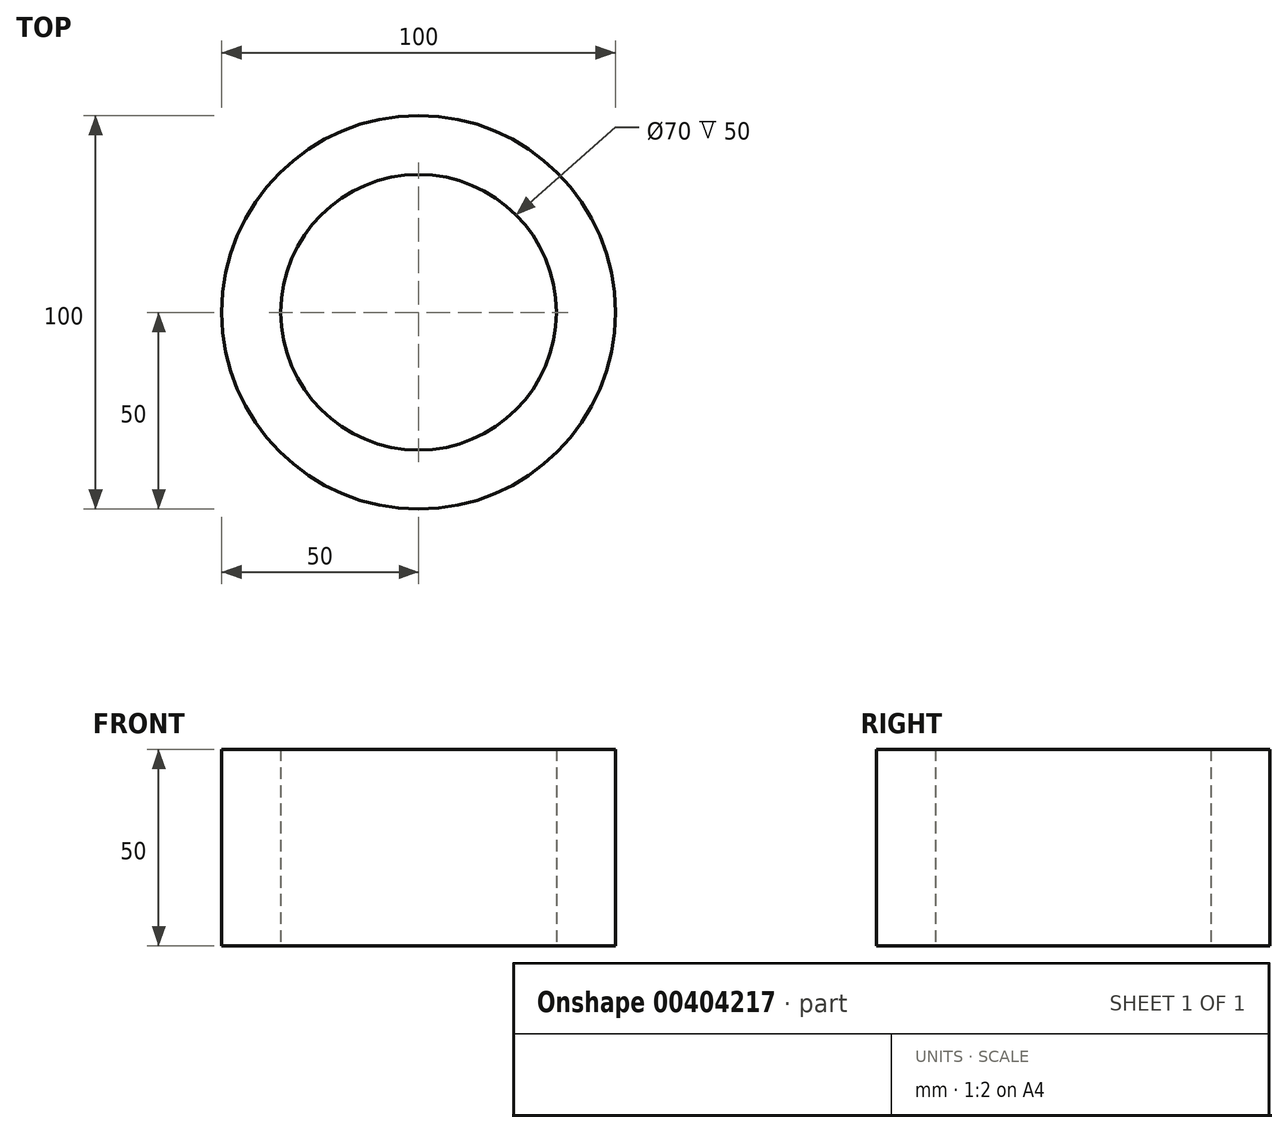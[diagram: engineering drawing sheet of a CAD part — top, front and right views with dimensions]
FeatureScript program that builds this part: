
annotation { "Feature Type Name" : "Feature", "Feature Type Description" : "" }
export const myFeature = defineFeature(function(context is Context, id is Id, definition is map)
    precondition{}
    {
        {
            var Q0;
            Q0=qCreatedBy(makeId("Top.planeOp"),FACE);
            var sketch = newSketch(context, id + "F0", { "sketchPlane" : qUnion([Q0])});
            skCircle(sketch, "E0", {"center": v(0, 0) * mm, "radius": 35 * mm});
            skCircle(sketch, "E1", {"center": v(0, 0) * mm, "radius": 50 * mm});
            skSolve(sketch);
        }
        {
            var Q0;
            Q0=makeQuery(id+"F0.imprint","IMPRINT",FACE,{"disambiguationData":[TD([[makeQuery(id+"F0.imprint","IMPRINT",EDGE,{"derivedFrom":sQuery(id+"F0.wireOp",EDGE,"E0")}),-1.0]])]});
            extrude(context, id + "F1", {"entities" : qUnion([Q0]), "depth" : 50 * mm});
        }
    });
